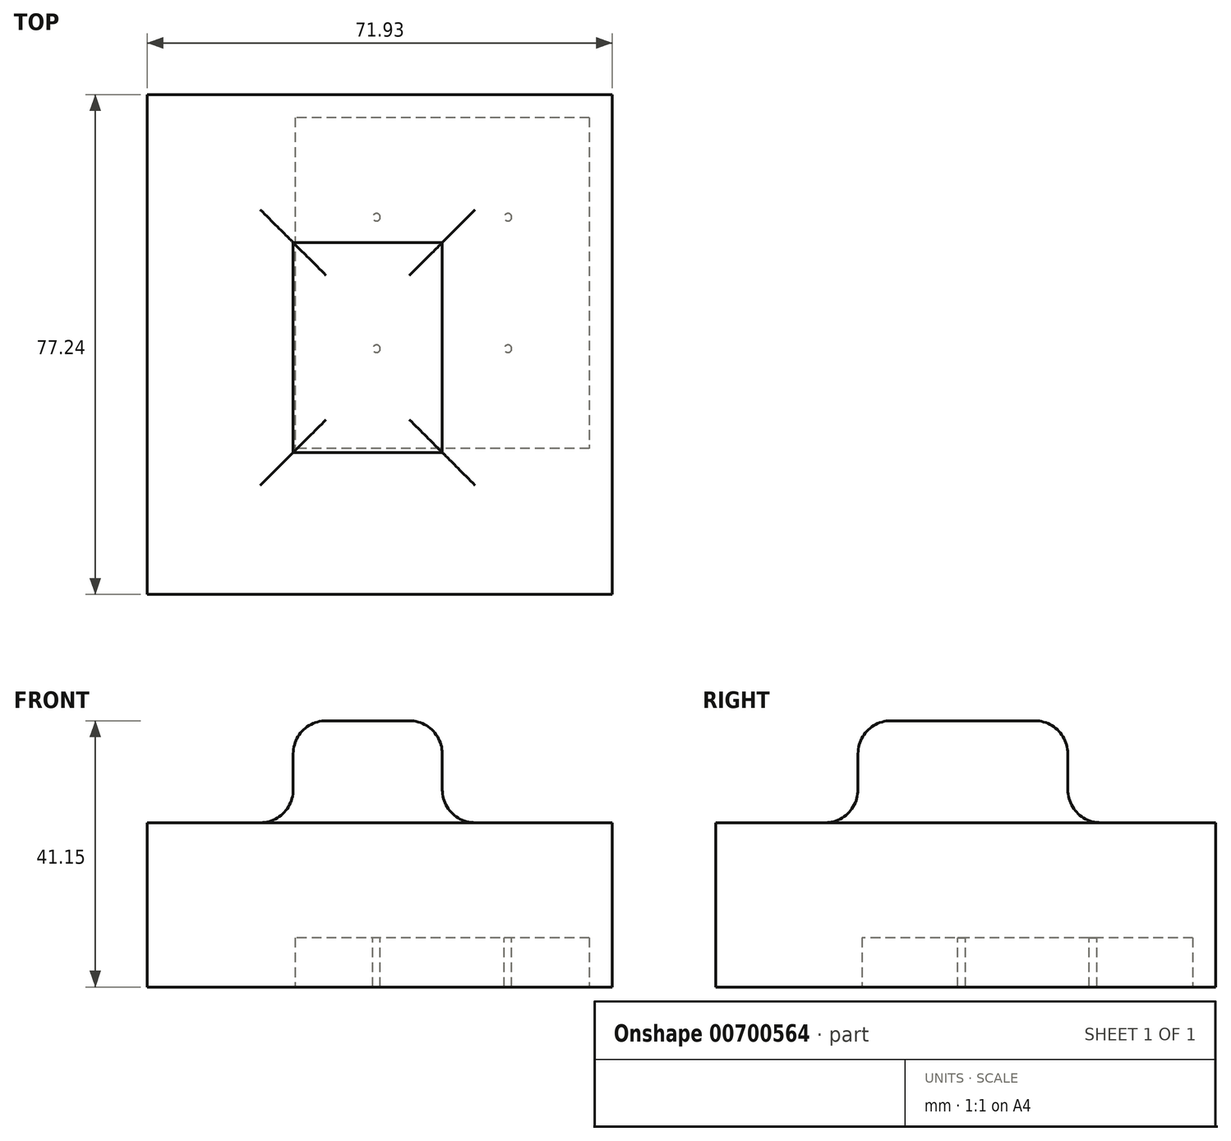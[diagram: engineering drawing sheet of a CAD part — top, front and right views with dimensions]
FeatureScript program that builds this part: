
annotation { "Feature Type Name" : "Feature", "Feature Type Description" : "" }
export const myFeature = defineFeature(function(context is Context, id is Id, definition is map)
    precondition{}
    {
        {
            var Q0;
            Q0=qCreatedBy(makeId("Top.planeOp"),FACE);
            var sketch = newSketch(context, id + "F0", { "sketchPlane" : qUnion([Q0])});
            skLineSegment(sketch, "E0.bottom", {"start": v(-23.04, 6.24) * mm, "end": v(0, 6.24) * mm});
            skLineSegment(sketch, "E0.top", {"start": v(-23.04, -26.2) * mm, "end": v(0, -26.2) * mm});
            skLineSegment(sketch, "E0.left", {"start": v(-23.04, 6.24) * mm, "end": v(-23.04, -26.2) * mm});
            skLineSegment(sketch, "E0.right", {"start": v(0, 6.24) * mm, "end": v(0, -26.2) * mm});
            skSolve(sketch);
        }
        {
            var Q0;
            Q0=makeQuery(id+"F0.imprint","IMPRINT",FACE,{"disambiguationData":[TD([[makeQuery(id+"F0.imprint","IMPRINT",EDGE,{"derivedFrom":sQuery(id+"F0.wireOp",EDGE,"E0.bottom")}),-1.0]])]});
            extrude(context, id + "F1", {"entities" : qUnion([Q0]), "depth" : 41.15 * mm, "offsetDistance" : 25.4 * mm});
        }
        {
            var Q0;
            Q0=qCreatedBy(makeId("Top.planeOp"),FACE);
            var sketch = newSketch(context, id + "F2", { "sketchPlane" : qUnion([Q0])});
            skLineSegment(sketch, "E1.bottom", {"start": v(-45.63, 29.09) * mm, "end": v(26.3, 29.09) * mm});
            skLineSegment(sketch, "E1.top", {"start": v(-45.63, -48.15) * mm, "end": v(26.3, -48.15) * mm});
            skLineSegment(sketch, "E1.left", {"start": v(-45.63, 29.09) * mm, "end": v(-45.63, -48.15) * mm});
            skLineSegment(sketch, "E1.right", {"start": v(26.3, 29.09) * mm, "end": v(26.3, -48.15) * mm});
            skSolve(sketch);
        }
        {
            var Q0;
            Q0=makeQuery(id+"F2.imprint","IMPRINT",FACE,{"disambiguationData":[TD([[makeQuery(id+"F2.imprint","IMPRINT",EDGE,{"derivedFrom":sQuery(id+"F2.wireOp",EDGE,"E1.bottom")}),-1.0]])]});
            extrude(context, id + "F3", {"entities" : qUnion([Q0]), "operationType" : NewBodyOperationType.ADD, "depth" : 25.4 * mm, "offsetDistance" : 25.4 * mm});
        }
        {
            var Q0;
            Q0=makeQuery(id+"F3.boolean.opBoolean","INTERSECT",EDGE,{"derivedFrom":[makeQuery(id+"F1.opExtrude","SWEPT_FACE",FACE,{"disambiguationData":[OSD([sQuery(id+"F0.wireOp",EDGE,"E0.left")])]}),makeQuery(id+"F3.opExtrude","CAP_FACE",FACE,{"disambiguationData":[OSD([sQuery(id+"F2.wireOp",EDGE,"E1.bottom"),sQuery(id+"F2.wireOp",EDGE,"E1.top"),sQuery(id+"F2.wireOp",EDGE,"E1.left"),sQuery(id+"F2.wireOp",EDGE,"E1.right")])],"isStart":false})]});
            var Q1;
            Q1=makeQuery(id+"F3.boolean.opBoolean","INTERSECT",EDGE,{"derivedFrom":[makeQuery(id+"F1.opExtrude","SWEPT_FACE",FACE,{"disambiguationData":[OSD([sQuery(id+"F0.wireOp",EDGE,"E0.top")])]}),makeQuery(id+"F3.opExtrude","CAP_FACE",FACE,{"disambiguationData":[OSD([sQuery(id+"F2.wireOp",EDGE,"E1.bottom"),sQuery(id+"F2.wireOp",EDGE,"E1.top"),sQuery(id+"F2.wireOp",EDGE,"E1.left"),sQuery(id+"F2.wireOp",EDGE,"E1.right")])],"isStart":false})]});
            var Q2;
            Q2=makeQuery(id+"F3.boolean.opBoolean","INTERSECT",EDGE,{"derivedFrom":[makeQuery(id+"F1.opExtrude","SWEPT_FACE",FACE,{"disambiguationData":[OSD([sQuery(id+"F0.wireOp",EDGE,"E0.right")])]}),makeQuery(id+"F3.opExtrude","CAP_FACE",FACE,{"disambiguationData":[OSD([sQuery(id+"F2.wireOp",EDGE,"E1.bottom"),sQuery(id+"F2.wireOp",EDGE,"E1.top"),sQuery(id+"F2.wireOp",EDGE,"E1.left"),sQuery(id+"F2.wireOp",EDGE,"E1.right")])],"isStart":false})]});
            var Q3;
            Q3=makeQuery(id+"F3.boolean.opBoolean","INTERSECT",EDGE,{"derivedFrom":[makeQuery(id+"F1.opExtrude","SWEPT_FACE",FACE,{"disambiguationData":[OSD([sQuery(id+"F0.wireOp",EDGE,"E0.bottom")])]}),makeQuery(id+"F3.opExtrude","CAP_FACE",FACE,{"disambiguationData":[OSD([sQuery(id+"F2.wireOp",EDGE,"E1.bottom"),sQuery(id+"F2.wireOp",EDGE,"E1.top"),sQuery(id+"F2.wireOp",EDGE,"E1.left"),sQuery(id+"F2.wireOp",EDGE,"E1.right")])],"isStart":false})]});
            var Q4;
            Q4=makeQuery(id+"F1.opExtrude","CAP_FACE",FACE,{"disambiguationData":[OSD([sQuery(id+"F0.wireOp",EDGE,"E0.bottom"),sQuery(id+"F0.wireOp",EDGE,"E0.top"),sQuery(id+"F0.wireOp",EDGE,"E0.left"),sQuery(id+"F0.wireOp",EDGE,"E0.right")])],"isStart":false});
            fillet(context, id + "F4", {"entities" : qUnion([Q0, Q1, Q2, Q3, Q4]), "tangentPropagation" : true, "radius" : 5.08 * mm, "defaultsChanged" : false, "vertexSettings" : [], "allowEdgeOverflow" : false});
        }
        {
            var Q0;
            Q0=qCreatedBy(makeId("Top.planeOp"),FACE);
            var sketch = newSketch(context, id + "F5", { "sketchPlane" : qUnion([Q0])});
            skLineSegment(sketch, "E2.bottom", {"start": v(22.72, 25.57) * mm, "end": v(-22.72, 25.57) * mm});
            skLineSegment(sketch, "E2.top", {"start": v(22.72, -25.57) * mm, "end": v(-22.72, -25.57) * mm});
            skLineSegment(sketch, "E2.left", {"start": v(22.72, 25.57) * mm, "end": v(22.72, -25.57) * mm});
            skLineSegment(sketch, "E2.right", {"start": v(-22.72, 25.57) * mm, "end": v(-22.72, -25.57) * mm});
            skPoint(sketch, "E2.middle", {"position": v(0, 0) * mm});
            skSolve(sketch);
        }
        {
            var Q0;
            Q0=makeQuery(id+"F5.imprint","IMPRINT",FACE,{"disambiguationData":[TD([[makeQuery(id+"F5.imprint","IMPRINT",EDGE,{"derivedFrom":sQuery(id+"F5.wireOp",EDGE,"E2.bottom")}),1.0]])]});
            extrude(context, id + "F6", {"entities" : qUnion([Q0]), "depth" : 7.62 * mm, "offsetDistance" : 25.4 * mm});
        }
        {
            var Q0;
            Q0=makeQuery(id+"F6.opExtrude","CAP_FACE",FACE,{"disambiguationData":[OSD([sQuery(id+"F5.wireOp",EDGE,"E2.bottom"),sQuery(id+"F5.wireOp",EDGE,"E2.top"),sQuery(id+"F5.wireOp",EDGE,"E2.left"),sQuery(id+"F5.wireOp",EDGE,"E2.right")])],"isStart":false});
            var sketch = newSketch(context, id + "F7", { "sketchPlane" : qUnion([Q0])});
            skLineSegment(sketch, "E3.bottom", {"start": v(10.16, 10.16) * mm, "end": v(-10.16, 10.16) * mm, "construction": true});
            skLineSegment(sketch, "E3.top", {"start": v(10.16, -10.16) * mm, "end": v(-10.16, -10.16) * mm, "construction": true});
            skLineSegment(sketch, "E3.left", {"start": v(10.16, 10.16) * mm, "end": v(10.16, -10.16) * mm, "construction": true});
            skLineSegment(sketch, "E3.right", {"start": v(-10.16, 10.16) * mm, "end": v(-10.16, -10.16) * mm, "construction": true});
            skPoint(sketch, "E3.middle", {"position": v(0, 0) * mm});
            skCircle(sketch, "E4", {"center": v(10.16, 10.16) * mm, "radius": 0.58 * mm});
            skCircle(sketch, "E5.1.0", {"center": v(10.16, -10.16) * mm, "radius": 0.58 * mm});
            skCircle(sketch, "E5.2.0", {"center": v(-10.16, -10.16) * mm, "radius": 0.58 * mm});
            skCircle(sketch, "E5.3.0", {"center": v(-10.16, 10.16) * mm, "radius": 0.58 * mm});
            skLineSegment(sketch, "E5.anchor1", {"start": v(0, 0) * mm, "end": v(10.16, 10.16) * mm, "construction": true});
            skLineSegment(sketch, "E5.anchor2", {"start": v(0, 0) * mm, "end": v(-10.16, 10.16) * mm, "construction": true});
            skSolve(sketch);
        }
        {
            var Q0;
            Q0=makeQuery(id+"F7.imprint","IMPRINT",FACE,{"disambiguationData":[TD([[makeQuery(id+"F7.imprint","IMPRINT",EDGE,{"derivedFrom":sQuery(id+"F7.wireOp",EDGE,"E5.1.0")}),1.0]])]});
            var Q1;
            Q1=makeQuery(id+"F7.imprint","IMPRINT",FACE,{"disambiguationData":[TD([[makeQuery(id+"F7.imprint","IMPRINT",EDGE,{"derivedFrom":sQuery(id+"F7.wireOp",EDGE,"E4")}),1.0]])]});
            var Q2;
            Q2=makeQuery(id+"F7.imprint","IMPRINT",FACE,{"disambiguationData":[TD([[makeQuery(id+"F7.imprint","IMPRINT",EDGE,{"derivedFrom":sQuery(id+"F7.wireOp",EDGE,"E5.3.0")}),1.0]])]});
            var Q3;
            Q3=makeQuery(id+"F7.imprint","IMPRINT",FACE,{"disambiguationData":[TD([[makeQuery(id+"F7.imprint","IMPRINT",EDGE,{"derivedFrom":sQuery(id+"F7.wireOp",EDGE,"E5.2.0")}),1.0]])]});
            var Q4;
            Q4=sQuery(id+"F7.wireOp",EDGE,"E5.3.0");
            var Q5;
            Q5=sQuery(id+"F7.wireOp",EDGE,"E4");
            var Q6;
            Q6=sQuery(id+"F7.wireOp",EDGE,"E5.1.0");
            var Q7;
            Q7=sQuery(id+"F7.wireOp",EDGE,"E5.2.0");
            extrude(context, id + "F8", {"entities" : qUnion([Q0, Q1, Q2, Q3]), "operationType" : NewBodyOperationType.REMOVE, "surfaceEntities" : qUnion([Q4, Q5, Q6, Q7]), "endBound" : BoundingType.UP_TO_NEXT, "oppositeDirection" : true, "depth" : 25.4 * mm, "offsetDistance" : 25.4 * mm});
        }
    });
